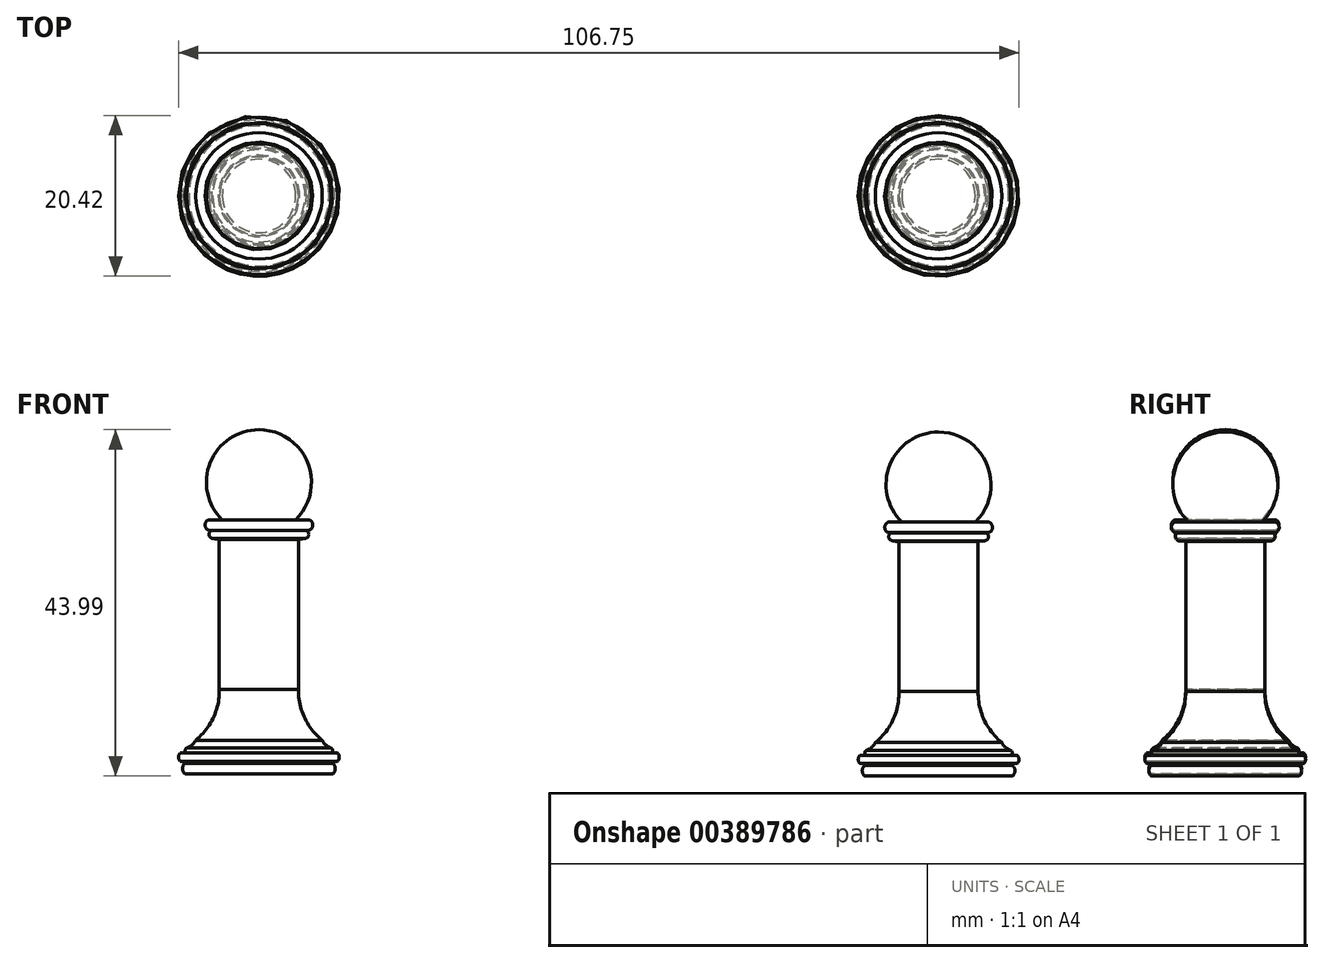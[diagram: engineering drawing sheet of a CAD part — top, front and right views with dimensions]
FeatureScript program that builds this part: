
annotation { "Feature Type Name" : "Feature", "Feature Type Description" : "" }
export const myFeature = defineFeature(function(context is Context, id is Id, definition is map)
    precondition{}
    {
        {
            var Q0;
            Q0=qCreatedBy(makeId("Front.planeOp"),FACE);
            var sketch = newSketch(context, id + "F0", { "sketchPlane" : qUnion([Q0])});
            skLineSegment(sketch, "E0", {"start": v(0, 0) * mm, "end": v(9.4, 0) * mm});
            skLineSegment(sketch, "E1", {"start": v(0, 0) * mm, "end": v(0, 30.36) * mm});
            skLineSegment(sketch, "E2", {"start": v(9.4, 1.33) * mm, "end": v(8.9, 1.33) * mm});
            skLineSegment(sketch, "E3", {"start": v(8.9, 1.33) * mm, "end": v(8.9, 1.59) * mm});
            skLineSegment(sketch, "E4", {"start": v(8.9, 1.59) * mm, "end": v(10, 1.59) * mm});
            skLineSegment(sketch, "E5", {"start": v(10, 2.62) * mm, "end": v(9.16, 2.62) * mm});
            skPoint(sketch, "E6", {"position": v(9.4, 1.33) * mm});
            skArc(sketch, "E7", {"start": v(9.4, 0) * mm, "mid": v(9.7, 0.66) * mm, "end": v(9.4, 1.33) * mm});
            skArc(sketch, "E8", {"start": v(10, 1.59) * mm, "mid": v(10.2, 2.1) * mm, "end": v(10, 2.62) * mm});
            skArc(sketch, "E9", {"start": v(8.01, 4.3) * mm, "mid": v(8.02, 4.28) * mm, "end": v(8.04, 4.26) * mm});
            skArc(sketch, "E10", {"start": v(8.01, 4.3) * mm, "mid": v(8.47, 3.67) * mm, "end": v(9.16, 3.28) * mm});
            skArc(sketch, "E11", {"start": v(9.16, 2.62) * mm, "mid": v(9.36, 2.95) * mm, "end": v(9.16, 3.28) * mm});
            skPoint(sketch, "E11.startSnap0", {"position": v(9.45, 2.62) * mm});
            skLineSegment(sketch, "E12", {"start": v(0, 29.89) * mm, "end": v(0, 30.36) * mm});
            skLineSegment(sketch, "E13", {"start": v(6.4, 30.93) * mm, "end": v(6.4, 30.93) * mm});
            skArc(sketch, "E14", {"start": v(5.87, 29.89) * mm, "mid": v(6.33, 30.32) * mm, "end": v(6.03, 30.89) * mm});
            skArc(sketch, "E15", {"start": v(6.03, 30.89) * mm, "mid": v(6.82, 31.41) * mm, "end": v(6.4, 32.26) * mm});
            skLineSegment(sketch, "E16.trimOffspring", {"start": v(5.87, 32.26) * mm, "end": v(4.66, 32.26) * mm});
            skLineSegment(sketch, "E17", {"start": v(5.87, 32.26) * mm, "end": v(6.4, 32.26) * mm});
            skPoint(sketch, "E18.end.orphan", {"position": v(5.87, 30.93) * mm});
            skArc(sketch, "E19", {"start": v(4.66, 32.26) * mm, "mid": v(6.18, 39.55) * mm, "end": v(0, 43.7) * mm});
            skLineSegment(sketch, "E20", {"start": v(0, 30.36) * mm, "end": v(0, 43.7) * mm});
            skArc(sketch, "E21", {"start": v(5.03, 10.73) * mm, "mid": v(5.78, 7.14) * mm, "end": v(8.04, 4.26) * mm});
            skLineSegment(sketch, "E22", {"start": v(5.17, 29.78) * mm, "end": v(5.87, 29.89) * mm});
            skLineSegment(sketch, "E23", {"start": v(5.03, 10.73) * mm, "end": v(5.03, 29.78) * mm});
            skLineSegment(sketch, "E24", {"start": v(5.17, 29.78) * mm, "end": v(5.03, 29.78) * mm});
            skLineSegment(sketch, "E25", {"start": v(-86.33, 0.3) * mm, "end": v(-76.93, 0.3) * mm});
            skLineSegment(sketch, "E26", {"start": v(-86.33, 0.3) * mm, "end": v(-86.33, 30.65) * mm});
            skLineSegment(sketch, "E27", {"start": v(-76.93, 1.62) * mm, "end": v(-77.44, 1.62) * mm});
            skLineSegment(sketch, "E28", {"start": v(-77.44, 1.62) * mm, "end": v(-77.44, 1.88) * mm});
            skLineSegment(sketch, "E29", {"start": v(-77.44, 1.88) * mm, "end": v(-76.33, 1.88) * mm});
            skLineSegment(sketch, "E30", {"start": v(-76.33, 2.9) * mm, "end": v(-77.18, 2.9) * mm});
            skPoint(sketch, "E31", {"position": v(-76.93, 1.62) * mm});
            skArc(sketch, "E32", {"start": v(-76.93, 0.3) * mm, "mid": v(-76.63, 0.96) * mm, "end": v(-76.93, 1.62) * mm});
            skArc(sketch, "E33", {"start": v(-76.33, 1.88) * mm, "mid": v(-76.12, 2.4) * mm, "end": v(-76.33, 2.9) * mm});
            skArc(sketch, "E34", {"start": v(-78.32, 4.6) * mm, "mid": v(-78.3, 4.57) * mm, "end": v(-78.3, 4.55) * mm});
            skArc(sketch, "E35", {"start": v(-78.32, 4.6) * mm, "mid": v(-77.86, 3.97) * mm, "end": v(-77.18, 3.57) * mm});
            skArc(sketch, "E36", {"start": v(-77.18, 2.9) * mm, "mid": v(-76.97, 3.24) * mm, "end": v(-77.18, 3.57) * mm});
            skPoint(sketch, "E36.startSnap0", {"position": v(-76.88, 2.9) * mm});
            skLineSegment(sketch, "E37", {"start": v(-86.33, 30.18) * mm, "end": v(-86.33, 30.65) * mm});
            skLineSegment(sketch, "E38", {"start": v(-79.94, 31.22) * mm, "end": v(-79.94, 31.22) * mm});
            skArc(sketch, "E39", {"start": v(-80.47, 30.18) * mm, "mid": v(-80, 30.62) * mm, "end": v(-80.3, 31.18) * mm});
            skArc(sketch, "E40", {"start": v(-80.3, 31.18) * mm, "mid": v(-79.51, 31.7) * mm, "end": v(-79.94, 32.55) * mm});
            skLineSegment(sketch, "E41.trimOffspring", {"start": v(-80.47, 32.55) * mm, "end": v(-81.67, 32.55) * mm});
            skLineSegment(sketch, "E42", {"start": v(-80.47, 32.55) * mm, "end": v(-79.94, 32.55) * mm});
            skPoint(sketch, "E43.end.orphan", {"position": v(-80.47, 31.22) * mm});
            skArc(sketch, "E44", {"start": v(-81.67, 32.55) * mm, "mid": v(-80.15, 39.84) * mm, "end": v(-86.33, 44) * mm});
            skLineSegment(sketch, "E45", {"start": v(-86.33, 30.65) * mm, "end": v(-86.33, 44) * mm});
            skArc(sketch, "E46", {"start": v(-81.3, 11.02) * mm, "mid": v(-80.55, 7.44) * mm, "end": v(-78.3, 4.55) * mm});
            skLineSegment(sketch, "E47", {"start": v(-81.16, 30.07) * mm, "end": v(-80.47, 30.18) * mm});
            skLineSegment(sketch, "E48", {"start": v(-81.3, 11.02) * mm, "end": v(-81.3, 30.07) * mm});
            skLineSegment(sketch, "E49", {"start": v(-81.16, 30.07) * mm, "end": v(-81.3, 30.07) * mm});
            skSolve(sketch);
        }
        {
            var Q0;
            Q0=makeQuery(id+"F0.imprint","IMPRINT",FACE,{"disambiguationData":[TD([[makeQuery(id+"F0.imprint","IMPRINT",EDGE,{"derivedFrom":sQuery(id+"F0.wireOp",EDGE,"E0")}),1.0]])]});
            var Q1;
            Q1=sQuery(id+"F0.wireOp",EDGE,"E1");
            revolve(context, id + "F1", {"entities" : qUnion([Q0]), "axis" : qUnion([Q1]), "revolveType" : RevolveType.FULL});
        }
        {
            var Q0;
            Q0=makeQuery(id+"F0.imprint","IMPRINT",FACE,{"disambiguationData":[TD([[makeQuery(id+"F0.imprint","IMPRINT",EDGE,{"derivedFrom":sQuery(id+"F0.wireOp",EDGE,"E25")}),1.0]])]});
            var Q1;
            Q1=sQuery(id+"F0.wireOp",EDGE,"E26");
            revolve(context, id + "F2", {"entities" : qUnion([Q0]), "axis" : qUnion([Q1]), "revolveType" : RevolveType.FULL});
        }
    });
